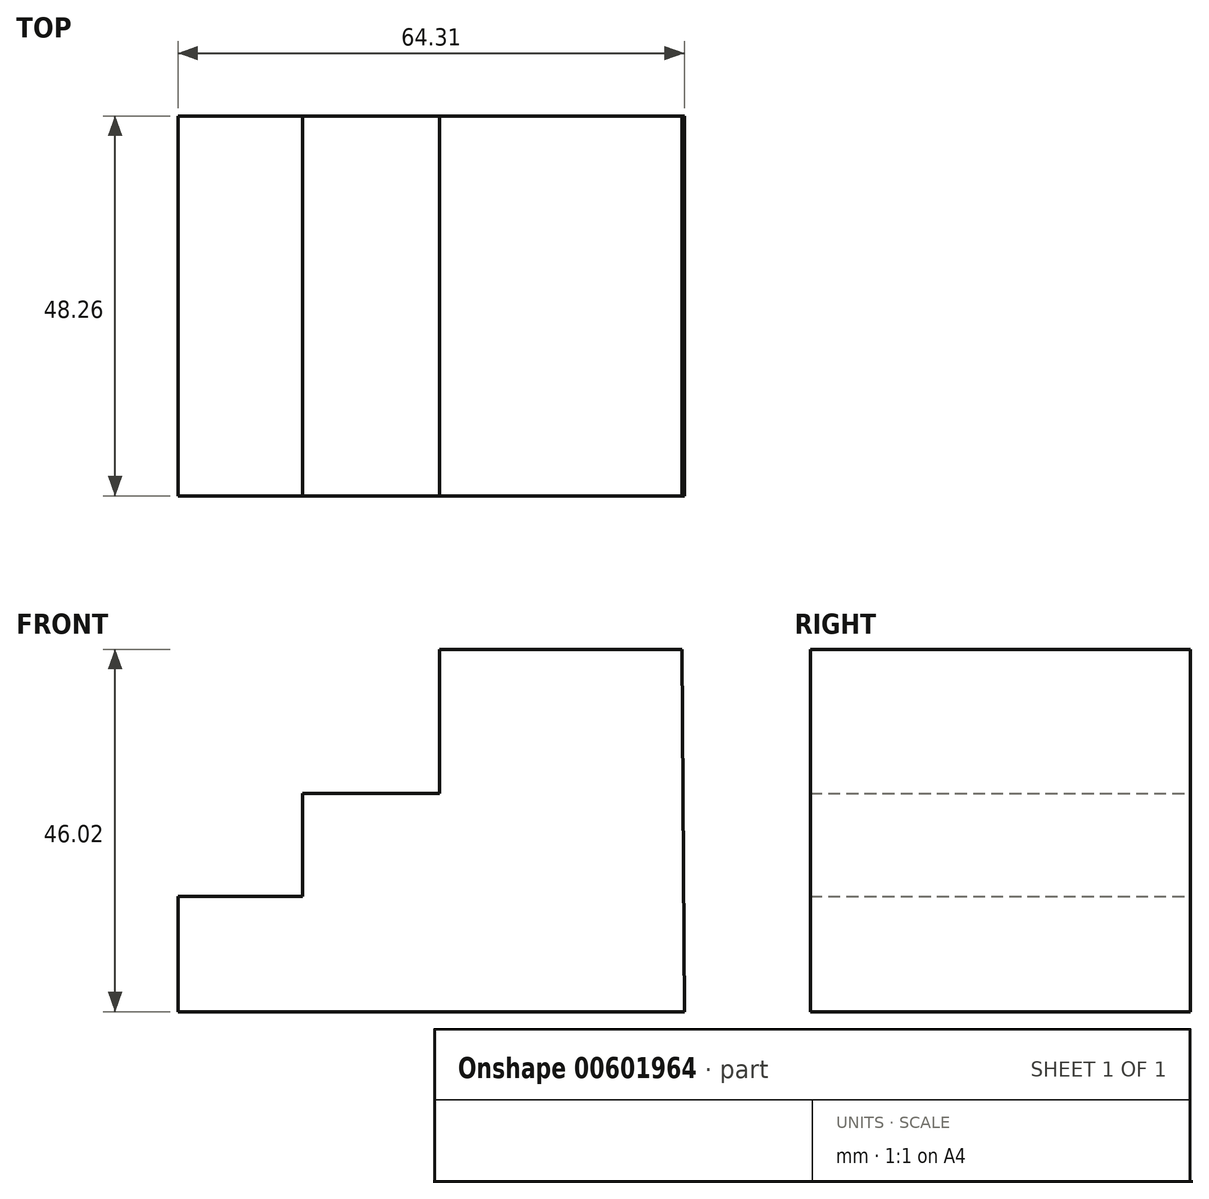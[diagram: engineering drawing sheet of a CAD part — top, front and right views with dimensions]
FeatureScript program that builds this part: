
annotation { "Feature Type Name" : "Feature", "Feature Type Description" : "" }
export const myFeature = defineFeature(function(context is Context, id is Id, definition is map)
    precondition{}
    {
        {
            var Q0;
            Q0=qCreatedBy(makeId("Front.planeOp"),FACE);
            var sketch = newSketch(context, id + "F0", { "sketchPlane" : qUnion([Q0])});
            skLineSegment(sketch, "E0", {"start": v(-50.14, -14.63) * mm, "end": v(-50.14, 0) * mm});
            skLineSegment(sketch, "E1", {"start": v(-50.14, 0) * mm, "end": v(-34.3, 0) * mm});
            skLineSegment(sketch, "E2", {"start": v(-34.3, 0) * mm, "end": v(-34.3, 13.1) * mm});
            skLineSegment(sketch, "E3", {"start": v(-34.3, 13.1) * mm, "end": v(-16.92, 13.1) * mm});
            skLineSegment(sketch, "E4", {"start": v(-16.92, 13.1) * mm, "end": v(-16.92, 31.4) * mm});
            skLineSegment(sketch, "E5", {"start": v(-16.92, 31.4) * mm, "end": v(13.87, 31.4) * mm});
            skLineSegment(sketch, "E6", {"start": v(-50.14, -14.63) * mm, "end": v(14.17, -14.63) * mm});
            skLineSegment(sketch, "E7", {"start": v(13.87, 31.4) * mm, "end": v(14.17, -14.63) * mm});
            skSolve(sketch);
        }
        {
            var Q0;
            Q0 = qSketchRegion(id + "F0", true);
            extrude(context, id + "F1", {"entities" : qUnion([Q0]), "depth" : 48.26 * mm, "offsetDistance" : 25.4 * mm});
        }
    });
